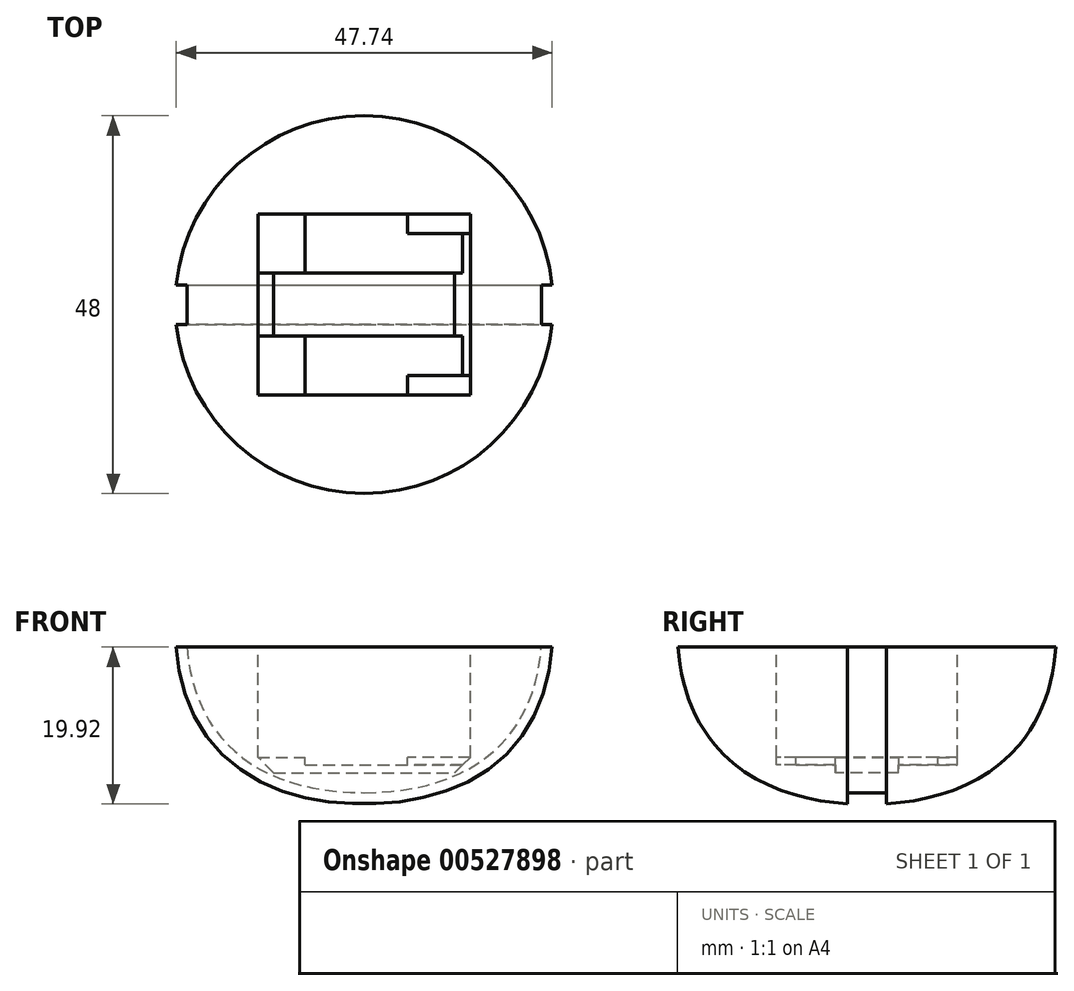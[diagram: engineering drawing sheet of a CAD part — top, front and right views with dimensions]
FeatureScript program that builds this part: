
annotation { "Feature Type Name" : "Feature", "Feature Type Description" : "" }
export const myFeature = defineFeature(function(context is Context, id is Id, definition is map)
    precondition{}
    {
        {
            var Q0;
            Q0=qCreatedBy(makeId("Front.planeOp"),FACE);
            var sketch = newSketch(context, id + "F0", { "sketchPlane" : qUnion([Q0])});
            skLineSegment(sketch, "E0", {"start": v(0, 0) * mm, "end": v(0, 60) * mm});
            skLineSegment(sketch, "E1", {"start": v(0, 0) * mm, "end": v(0, 20) * mm, "construction": true});
            skLineSegment(sketch, "E2", {"start": v(0, 20) * mm, "end": v(24, 20) * mm});
            skLineSegment(sketch, "E3", {"start": v(0, 60) * mm, "end": v(14, 60) * mm, "construction": true});
            skLineSegment(sketch, "E4", {"start": v(0, 0) * mm, "end": v(14, 0) * mm, "construction": true});
            skFitSpline(sketch, "E5", {"points": [v(0, 0) * mm, v(24, 20) * mm, v(0, 60) * mm], "startDerivative": vector(93.32, 0) * mm, "endDerivative": vector(-76.37, 0) * mm});
            skFitSpline(sketch, "E6.MirrorCS", {"points": [v(0, 0) * mm, v(-24, 20) * mm, v(0, 60) * mm], "startDerivative": vector(-93.32, 0) * mm, "endDerivative": vector(76.37, 0) * mm});
            skSolve(sketch);
        }
        {
            var Q0;
            {var subQ3=sQuery(id+"F0.wireOp",EDGE,"E2");Q0=makeQuery(id+"F0.imprint","IMPRINT",FACE,{"disambiguationData":[TD([[makeQuery(id+"F0.imprint","IMPRINT",EDGE,{"derivedFrom":subQ3}),-1.0]])]});}
            var Q1;
            Q1=sQuery(id+"F0.wireOp",EDGE,"E0");
            revolve(context, id + "F1", {"entities" : qUnion([Q0]), "axis" : qUnion([Q1]), "revolveType" : RevolveType.FULL});
        }
        {
            var Q0;
            Q0=makeQuery(id+"F1.opRevolve","SWEPT_FACE",FACE,{"disambiguationData":[OSD([sQuery(id+"F0.wireOp",EDGE,"E2")])]});
            var sketch = newSketch(context, id + "F2", { "sketchPlane" : qUnion([Q0])});
            skLineSegment(sketch, "E7", {"start": v(0, 0) * mm, "end": v(13.5, 0) * mm, "construction": true});
            skLineSegment(sketch, "E8", {"start": v(13.5, 0) * mm, "end": v(13.5, 11.5) * mm});
            skLineSegment(sketch, "E9", {"start": v(13.5, 11.5) * mm, "end": v(-13.5, 11.5) * mm});
            skLineSegment(sketch, "E10", {"start": v(-13.5, 11.5) * mm, "end": v(-13.5, -11.5) * mm});
            skLineSegment(sketch, "E11", {"start": v(-13.5, -11.5) * mm, "end": v(13.5, -11.5) * mm});
            skLineSegment(sketch, "E12", {"start": v(13.5, -11.5) * mm, "end": v(13.5, 0) * mm});
            skSolve(sketch);
        }
        {
            var Q0;
            Q0=makeQuery(id+"F2.imprint","IMPRINT",FACE,{"disambiguationData":[TD([[makeQuery(id+"F2.imprint","IMPRINT",EDGE,{"derivedFrom":sQuery(id+"F2.wireOp",EDGE,"E8")}),1.0]])]});
            var Q1;
            Q1=qConstructionFilter(qBodyType(qCreatedBy(id+"F2",EDGE),BodyType.WIRE),ConstructionObject.NO);
            extrude(context, id + "F3", {"entities" : qUnion([Q0]), "operationType" : NewBodyOperationType.REMOVE, "surfaceEntities" : qUnion([Q1]), "oppositeDirection" : true, "depth" : 14 * mm});
        }
        {
            var Q0;
            Q0=makeQuery(id+"F3.boolean.opBoolean","COPY",FACE,{"derivedFrom":makeQuery(id+"F3.opExtrude","CAP_FACE",FACE,{"disambiguationData":[OSD([sQuery(id+"F2.wireOp",EDGE,"E8"),sQuery(id+"F2.wireOp",EDGE,"E9"),sQuery(id+"F2.wireOp",EDGE,"E10"),sQuery(id+"F2.wireOp",EDGE,"E11"),sQuery(id+"F2.wireOp",EDGE,"E12")])],"isStart":false})});
            var sketch = newSketch(context, id + "F4", { "sketchPlane" : qUnion([Q0])});
            skLineSegment(sketch, "E13", {"start": v(13.5, 0) * mm, "end": v(5.5, 0) * mm, "construction": true});
            skPoint(sketch, "E13.endSnap0", {"position": v(13.5, 0) * mm});
            skLineSegment(sketch, "E14", {"start": v(5.5, 9) * mm, "end": v(5.5, 11.5) * mm});
            skLineSegment(sketch, "E15", {"start": v(5.5, 11.5) * mm, "end": v(-7.5, 11.5) * mm});
            skLineSegment(sketch, "E16", {"start": v(-7.5, 11.5) * mm, "end": v(-7.5, -11.5) * mm});
            skLineSegment(sketch, "E17", {"start": v(-7.5, -11.5) * mm, "end": v(5.5, -11.5) * mm});
            skLineSegment(sketch, "E18", {"start": v(5.5, -9) * mm, "end": v(5.5, -11.5) * mm});
            skLineSegment(sketch, "E19", {"start": v(13.5, 0) * mm, "end": v(13.5, -9) * mm});
            skLineSegment(sketch, "E20", {"start": v(13.5, -9) * mm, "end": v(5.5, -9) * mm});
            skLineSegment(sketch, "E21", {"start": v(13.5, 0) * mm, "end": v(13.5, 9) * mm});
            skLineSegment(sketch, "E22", {"start": v(13.5, 9) * mm, "end": v(5.5, 9) * mm});
            skSolve(sketch);
        }
        {
            var Q0;
            Q0=qSketchRegion(id+"F4",true);
            extrude(context, id + "F5", {"entities" : qUnion([Q0]), "operationType" : NewBodyOperationType.REMOVE, "oppositeDirection" : true, "depth" : 1 * mm});
        }
        {
            var Q0;
            Q0=makeQuery(id+"F5.boolean.opBoolean","COPY",FACE,{"derivedFrom":makeQuery(id+"F5.opExtrude","CAP_FACE",FACE,{"disambiguationData":[OSD([sQuery(id+"F4.wireOp",EDGE,"E14"),sQuery(id+"F4.wireOp",EDGE,"E15"),sQuery(id+"F4.wireOp",EDGE,"E16"),sQuery(id+"F4.wireOp",EDGE,"E17"),sQuery(id+"F4.wireOp",EDGE,"E18"),sQuery(id+"F4.wireOp",EDGE,"E19"),sQuery(id+"F4.wireOp",EDGE,"E20"),sQuery(id+"F4.wireOp",EDGE,"E21"),sQuery(id+"F4.wireOp",EDGE,"E22")])],"isStart":false})});
            var sketch = newSketch(context, id + "F6", { "sketchPlane" : qUnion([Q0])});
            skLineSegment(sketch, "E23", {"start": v(13.5, 0) * mm, "end": v(13.5, 4) * mm});
            skLineSegment(sketch, "E24", {"start": v(13.5, 4) * mm, "end": v(-13.5, 4) * mm});
            skLineSegment(sketch, "E25", {"start": v(-13.5, 4) * mm, "end": v(-13.5, -4) * mm});
            skLineSegment(sketch, "E26", {"start": v(-13.5, -4) * mm, "end": v(13.5, -4) * mm});
            skLineSegment(sketch, "E27", {"start": v(13.5, -4) * mm, "end": v(13.5, 0) * mm});
            skSolve(sketch);
        }
        {
            var Q0;
            Q0=qSketchRegion(id+"F6",true);
            extrude(context, id + "F7", {"entities" : qUnion([Q0]), "operationType" : NewBodyOperationType.REMOVE, "oppositeDirection" : true, "depth" : 1 * mm, "hasSecondDirection" : true, "secondDirectionOppositeDirection" : false, "secondDirectionDepth" : 1 * mm});
        }
        {
            var Q0;
            Q0=qCreatedBy(makeId("Right.planeOp"),FACE);
            var sketch = newSketch(context, id + "F8", { "sketchPlane" : qUnion([Q0])});
            skLineSegment(sketch, "E28", {"start": v(0, 0) * mm, "end": v(2.5, 0) * mm});
            skLineSegment(sketch, "E29", {"start": v(2.5, 0) * mm, "end": v(2.5, 1.5) * mm});
            skLineSegment(sketch, "E30", {"start": v(2.5, 1.5) * mm, "end": v(-2.5, 1.5) * mm});
            skLineSegment(sketch, "E31", {"start": v(-2.5, 1.5) * mm, "end": v(-2.5, 0) * mm});
            skLineSegment(sketch, "E32", {"start": v(-2.5, 0) * mm, "end": v(0, 0) * mm});
            skSolve(sketch);
        }
        {
            var Q0;
            Q0=makeQuery(id+"F7.boolean.opBoolean","COPY",EDGE,{"derivedFrom":makeQuery(id+"F7.opExtrude","CAP_EDGE",EDGE,{"disambiguationData":[OSD([sQuery(id+"F6.wireOp",EDGE,"E25")])],"isStart":false})});
            var Q1;
            Q1=makeQuery(id+"F7.boolean.opBoolean","COPY",EDGE,{"derivedFrom":makeQuery(id+"F7.opExtrude","CAP_EDGE",EDGE,{"disambiguationData":[OSD([sQuery(id+"F6.wireOp",EDGE,"E23"),sQuery(id+"F6.wireOp",EDGE,"E27")])],"isStart":false})});
            chamfer(context, id + "F9", {"entities" : qUnion([Q0, Q1]), "width" : 2 * mm, "tangentPropagation" : true});
        }
        {
            var Q0;
            Q0=qSketchRegion(id+"F8",true);
            var Q1;
            Q1=sQuery(id+"F0.wireOp",EDGE,"E5");
            var Q2;
            Q2=sQuery(id+"F0.wireOp",EDGE,"E6.MirrorCS");
            sweep(context, id + "F10", {"operationType" : NewBodyOperationType.REMOVE, "profiles" : qUnion([Q0]), "path" : qUnion([Q1, Q2])});
        }
    });
